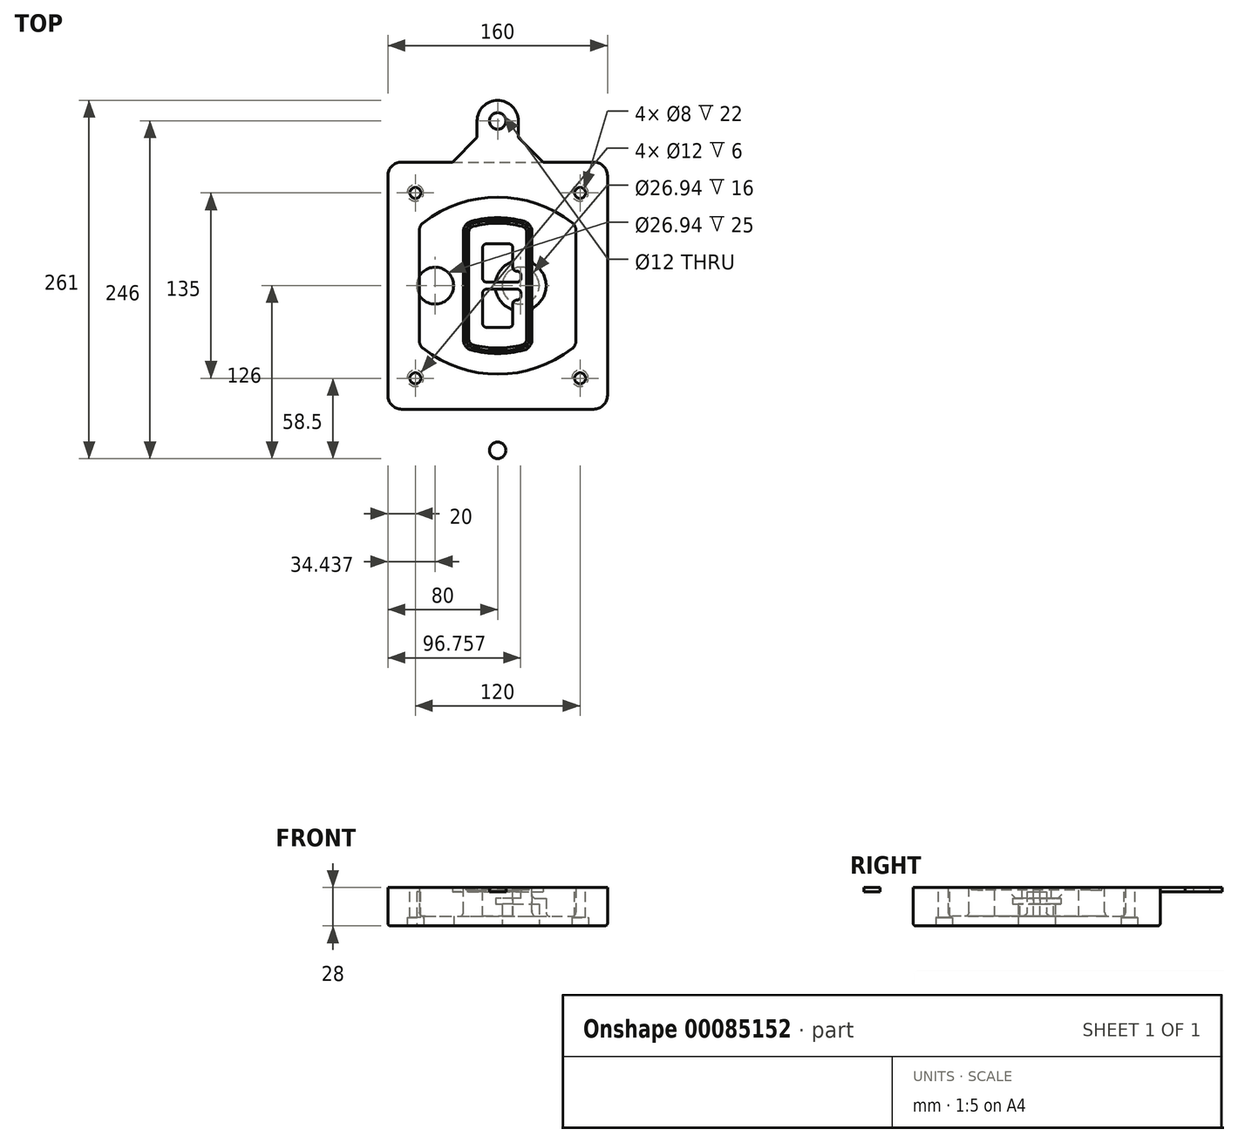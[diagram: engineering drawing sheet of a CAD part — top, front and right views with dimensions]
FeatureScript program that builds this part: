
annotation { "Feature Type Name" : "Feature", "Feature Type Description" : "" }
export const myFeature = defineFeature(function(context is Context, id is Id, definition is map)
    precondition{}
    {
        {
            var Q0;
            Q0=qCreatedBy(makeId("Top.planeOp"),FACE);
            var sketch = newSketch(context, id + "F0", { "sketchPlane" : qUnion([Q0])});
            skPoint(sketch, "E0.rect.middle", {"position": v(0, 0) * mm});
            skLineSegment(sketch, "E1.bottom", {"start": v(-70, -90) * mm, "end": v(70, -90) * mm});
            skLineSegment(sketch, "E1.top", {"start": v(-70, 90) * mm, "end": v(70, 90) * mm});
            skLineSegment(sketch, "E1.left", {"start": v(-80, -80) * mm, "end": v(-80, 80) * mm});
            skLineSegment(sketch, "E1.right", {"start": v(80, -80) * mm, "end": v(80, 80) * mm});
            skLineSegment(sketch, "E2", {"start": v(-80, 90) * mm, "end": v(80, -90) * mm, "construction": true});
            skLineSegment(sketch, "E3", {"start": v(80, 90) * mm, "end": v(-80, -90) * mm, "construction": true});
            skCircle(sketch, "E4", {"center": v(-60, 67.5) * mm, "radius": 4 * mm});
            skCircle(sketch, "E5", {"center": v(60, 67.5) * mm, "radius": 4 * mm});
            skCircle(sketch, "E6", {"center": v(60, -67.5) * mm, "radius": 4 * mm});
            skCircle(sketch, "E7", {"center": v(-60, -67.5) * mm, "radius": 4 * mm});
            skLineSegment(sketch, "E8", {"start": v(-60, 67.5) * mm, "end": v(60, 67.5) * mm, "construction": true});
            skLineSegment(sketch, "E9", {"start": v(60, 67.5) * mm, "end": v(60, -67.5) * mm, "construction": true});
            skLineSegment(sketch, "E10", {"start": v(60, -67.5) * mm, "end": v(-60, -67.5) * mm, "construction": true});
            skLineSegment(sketch, "E11", {"start": v(-60, -67.5) * mm, "end": v(-60, 67.5) * mm, "construction": true});
            skLineSegment(sketch, "E12", {"start": v(-60, 40.3) * mm, "end": v(-60, -40.3) * mm});
            skLineSegment(sketch, "E13", {"start": v(60, 40.3) * mm, "end": v(60, -40.3) * mm});
            skArc(sketch, "E14", {"start": v(56.15, 48.18) * mm, "mid": v(0, 67.5) * mm, "end": v(-56.15, 48.18) * mm});
            skArc(sketch, "E15", {"start": v(-56.15, -48.18) * mm, "mid": v(0, -67.5) * mm, "end": v(56.15, -48.18) * mm});
            skLineSegment(sketch, "E16", {"start": v(-60, 0) * mm, "end": v(60, 0) * mm, "construction": true});
            skPoint(sketch, "E17.visualSharp", {"position": v(-60, -45) * mm});
            skArc(sketch, "E17.filletArc", {"start": v(-60, -40.3) * mm, "mid": v(-58.99, -44.68) * mm, "end": v(-56.15, -48.18) * mm});
            skPoint(sketch, "E18.visualSharp", {"position": v(-60, 45) * mm});
            skArc(sketch, "E18.filletArc", {"start": v(-56.15, 48.18) * mm, "mid": v(-58.99, 44.68) * mm, "end": v(-60, 40.3) * mm});
            skPoint(sketch, "E19.visualSharp", {"position": v(60, 45) * mm});
            skArc(sketch, "E19.filletArc", {"start": v(60, 40.3) * mm, "mid": v(58.99, 44.68) * mm, "end": v(56.15, 48.18) * mm});
            skPoint(sketch, "E20.visualSharp", {"position": v(60, -45) * mm});
            skArc(sketch, "E20.filletArc", {"start": v(56.15, -48.18) * mm, "mid": v(58.99, -44.68) * mm, "end": v(60, -40.3) * mm});
            skPoint(sketch, "E21.visualSharp", {"position": v(-80, 90) * mm});
            skArc(sketch, "E21.filletArc", {"start": v(-70, 90) * mm, "mid": v(-77.07, 87.07) * mm, "end": v(-80, 80) * mm});
            skPoint(sketch, "E22.visualSharp", {"position": v(80, 90) * mm});
            skArc(sketch, "E22.filletArc", {"start": v(80, 80) * mm, "mid": v(77.07, 87.07) * mm, "end": v(70, 90) * mm});
            skPoint(sketch, "E23.visualSharp", {"position": v(80, -90) * mm});
            skArc(sketch, "E23.filletArc", {"start": v(70, -90) * mm, "mid": v(77.07, -87.07) * mm, "end": v(80, -80) * mm});
            skPoint(sketch, "E24.visualSharp", {"position": v(-80, -90) * mm});
            skArc(sketch, "E24.filletArc", {"start": v(-80, -80) * mm, "mid": v(-77.07, -87.07) * mm, "end": v(-70, -90) * mm});
            skArc(sketch, "E25.0", {"start": v(57, 40.3) * mm, "mid": v(56.3, 43.36) * mm, "end": v(54.3, 45.81) * mm});
            skLineSegment(sketch, "E25.1", {"start": v(57, 40.3) * mm, "end": v(57, -40.3) * mm});
            skArc(sketch, "E25.2", {"start": v(54.3, -45.81) * mm, "mid": v(56.3, -43.36) * mm, "end": v(57, -40.3) * mm});
            skArc(sketch, "E25.3", {"start": v(-54.3, -45.81) * mm, "mid": v(0, -64.5) * mm, "end": v(54.3, -45.81) * mm});
            skArc(sketch, "E25.4", {"start": v(-57, -40.3) * mm, "mid": v(-56.3, -43.36) * mm, "end": v(-54.3, -45.81) * mm});
            skArc(sketch, "E25.5", {"start": v(54.3, 45.81) * mm, "mid": v(0, 64.5) * mm, "end": v(-54.3, 45.81) * mm});
            skLineSegment(sketch, "E25.6", {"start": v(-57, 40.3) * mm, "end": v(-57, -40.3) * mm});
            skArc(sketch, "E25.7", {"start": v(-54.3, 45.81) * mm, "mid": v(-56.3, 43.36) * mm, "end": v(-57, 40.3) * mm});
            skArc(sketch, "E26.0", {"start": v(-58.62, 51.33) * mm, "mid": v(-62.58, 46.43) * mm, "end": v(-64, 40.3) * mm});
            skArc(sketch, "E26.1", {"start": v(58.62, 51.33) * mm, "mid": v(0, 71.5) * mm, "end": v(-58.62, 51.33) * mm});
            skArc(sketch, "E26.2", {"start": v(64, 40.3) * mm, "mid": v(62.58, 46.43) * mm, "end": v(58.62, 51.33) * mm});
            skLineSegment(sketch, "E26.3", {"start": v(64, 40.3) * mm, "end": v(64, -40.3) * mm});
            skArc(sketch, "E26.4", {"start": v(58.62, -51.33) * mm, "mid": v(62.58, -46.43) * mm, "end": v(64, -40.3) * mm});
            skLineSegment(sketch, "E26.5", {"start": v(-64, 40.3) * mm, "end": v(-64, -40.3) * mm});
            skArc(sketch, "E26.6", {"start": v(-58.62, -51.33) * mm, "mid": v(0, -71.5) * mm, "end": v(58.62, -51.33) * mm});
            skArc(sketch, "E26.7", {"start": v(-64, -40.3) * mm, "mid": v(-62.58, -46.43) * mm, "end": v(-58.62, -51.33) * mm});
            skSolve(sketch);
        }
        {
            var Q0;
            Q0=makeQuery(id+"F0.imprint","IMPRINT",FACE,{"disambiguationData":[TD([[makeQuery(id+"F0.imprint","IMPRINT",EDGE,{"derivedFrom":sQuery(id+"F0.wireOp",EDGE,"E1.bottom")}),1.0]])]});
            var Q1;
            Q1=makeQuery(id+"F0.imprint","IMPRINT",FACE,{"disambiguationData":[TD([[makeQuery(id+"F0.imprint","IMPRINT",EDGE,{"derivedFrom":sQuery(id+"F0.wireOp",EDGE,"E12")}),1.0]])]});
            var Q2;
            Q2=makeQuery(id+"F0.imprint","IMPRINT",FACE,{"disambiguationData":[TD([[makeQuery(id+"F0.imprint","IMPRINT",EDGE,{"derivedFrom":sQuery(id+"F0.wireOp",EDGE,"E25.0")}),1.0]])]});
            var Q3;
            Q3=makeQuery(id+"F0.imprint","IMPRINT",FACE,{"disambiguationData":[TD([[makeQuery(id+"F0.imprint","IMPRINT",EDGE,{"derivedFrom":sQuery(id+"F0.wireOp",EDGE,"E12")}),-1.0]])]});
            extrude(context, id + "F1", {"entities" : qUnion([Q0, Q1, Q2, Q3]), "oppositeDirection" : true, "depth" : 25 * mm});
        }
        {
            var Q0;
            Q0=makeQuery(id+"F0.imprint","IMPRINT",FACE,{"disambiguationData":[TD([[makeQuery(id+"F0.imprint","IMPRINT",EDGE,{"derivedFrom":sQuery(id+"F0.wireOp",EDGE,"E12")}),1.0]])]});
            extrude(context, id + "F2", {"entities" : qUnion([Q0]), "operationType" : NewBodyOperationType.ADD, "depth" : 3 * mm});
        }
        {
            var Q0;
            Q0=makeQuery(id+"F0.imprint","IMPRINT",FACE,{"disambiguationData":[TD([[makeQuery(id+"F0.imprint","IMPRINT",EDGE,{"derivedFrom":sQuery(id+"F0.wireOp",EDGE,"E25.0")}),1.0]])]});
            extrude(context, id + "F3", {"entities" : qUnion([Q0]), "operationType" : NewBodyOperationType.REMOVE, "oppositeDirection" : true, "depth" : 18 * mm});
        }
        {
            var Q0;
            Q0=makeQuery(id+"F2.opExtrude","CAP_FACE",FACE,{"disambiguationData":[OSD([sQuery(id+"F0.wireOp",EDGE,"E12"),sQuery(id+"F0.wireOp",EDGE,"E13"),sQuery(id+"F0.wireOp",EDGE,"E14"),sQuery(id+"F0.wireOp",EDGE,"E15"),sQuery(id+"F0.wireOp",EDGE,"E17.filletArc"),sQuery(id+"F0.wireOp",EDGE,"E18.filletArc"),sQuery(id+"F0.wireOp",EDGE,"E19.filletArc"),sQuery(id+"F0.wireOp",EDGE,"E20.filletArc"),sQuery(id+"F0.wireOp",EDGE,"E25.0"),sQuery(id+"F0.wireOp",EDGE,"E25.1"),sQuery(id+"F0.wireOp",EDGE,"E25.2"),sQuery(id+"F0.wireOp",EDGE,"E25.3"),sQuery(id+"F0.wireOp",EDGE,"E25.4"),sQuery(id+"F0.wireOp",EDGE,"E25.5"),sQuery(id+"F0.wireOp",EDGE,"E25.6"),sQuery(id+"F0.wireOp",EDGE,"E25.7")])],"isStart":false});
            var sketch = newSketch(context, id + "F4", { "sketchPlane" : qUnion([Q0])});
            skArc(sketch, "E27.0", {"start": v(-19.08, -46.97) * mm, "mid": v(0, -49.5) * mm, "end": v(19.08, -46.97) * mm});
            skArc(sketch, "E28.0", {"start": v(19.08, 46.97) * mm, "mid": v(0, 49.5) * mm, "end": v(-19.08, 46.97) * mm});
            skLineSegment(sketch, "E29", {"start": v(-25, 39.25) * mm, "end": v(-25, -39.25) * mm});
            skLineSegment(sketch, "E30", {"start": v(25, 39.25) * mm, "end": v(25, -39.25) * mm});
            skLineSegment(sketch, "E31", {"start": v(-25, 45.1) * mm, "end": v(25, 45.1) * mm, "construction": true});
            skLineSegment(sketch, "E32", {"start": v(-25, -45.1) * mm, "end": v(25, -45.1) * mm, "construction": true});
            skPoint(sketch, "E33.visualSharp", {"position": v(-25, 45.1) * mm});
            skArc(sketch, "E33.filletArc", {"start": v(-19.08, 46.97) * mm, "mid": v(-23.35, 44.11) * mm, "end": v(-25, 39.25) * mm});
            skPoint(sketch, "E34.visualSharp", {"position": v(25, 45.1) * mm});
            skArc(sketch, "E34.filletArc", {"start": v(25, 39.25) * mm, "mid": v(23.35, 44.11) * mm, "end": v(19.08, 46.97) * mm});
            skPoint(sketch, "E35.visualSharp", {"position": v(25, -45.1) * mm});
            skArc(sketch, "E35.filletArc", {"start": v(19.08, -46.97) * mm, "mid": v(23.35, -44.11) * mm, "end": v(25, -39.25) * mm});
            skPoint(sketch, "E36.visualSharp", {"position": v(-25, -45.1) * mm});
            skArc(sketch, "E36.filletArc", {"start": v(-25, -39.25) * mm, "mid": v(-23.35, -44.11) * mm, "end": v(-19.08, -46.97) * mm});
            skArc(sketch, "E37.0", {"start": v(54.3, 45.81) * mm, "mid": v(0, 64.5) * mm, "end": v(-54.3, 45.81) * mm});
            skArc(sketch, "E37.1", {"start": v(-54.3, 45.81) * mm, "mid": v(-56.3, 43.36) * mm, "end": v(-57, 40.3) * mm});
            skLineSegment(sketch, "E37.2", {"start": v(-57, 40.3) * mm, "end": v(-57, -40.3) * mm});
            skArc(sketch, "E37.3", {"start": v(-57, -40.3) * mm, "mid": v(-56.3, -43.36) * mm, "end": v(-54.3, -45.81) * mm});
            skArc(sketch, "E37.4", {"start": v(-54.3, -45.81) * mm, "mid": v(0, -64.5) * mm, "end": v(54.3, -45.81) * mm});
            skArc(sketch, "E37.5", {"start": v(54.3, -45.81) * mm, "mid": v(56.3, -43.36) * mm, "end": v(57, -40.3) * mm});
            skLineSegment(sketch, "E37.6", {"start": v(57, 40.3) * mm, "end": v(57, -40.3) * mm});
            skArc(sketch, "E37.7", {"start": v(57, 40.3) * mm, "mid": v(56.3, 43.36) * mm, "end": v(54.3, 45.81) * mm});
            skLineSegment(sketch, "E38.0", {"start": v(23, 39.25) * mm, "end": v(23, -39.25) * mm});
            skArc(sketch, "E38.1", {"start": v(18.56, -45.04) * mm, "mid": v(21.76, -42.9) * mm, "end": v(23, -39.25) * mm});
            skArc(sketch, "E38.2", {"start": v(-18.56, -45.04) * mm, "mid": v(0, -47.5) * mm, "end": v(18.56, -45.04) * mm});
            skArc(sketch, "E38.3", {"start": v(-23, -39.25) * mm, "mid": v(-21.76, -42.9) * mm, "end": v(-18.56, -45.04) * mm});
            skLineSegment(sketch, "E38.4", {"start": v(-23, 39.25) * mm, "end": v(-23, -39.25) * mm});
            skArc(sketch, "E38.5", {"start": v(23, 39.25) * mm, "mid": v(21.76, 42.9) * mm, "end": v(18.56, 45.04) * mm});
            skArc(sketch, "E38.6", {"start": v(-18.56, 45.04) * mm, "mid": v(-21.76, 42.9) * mm, "end": v(-23, 39.25) * mm});
            skArc(sketch, "E38.7", {"start": v(18.56, 45.04) * mm, "mid": v(0, 47.5) * mm, "end": v(-18.56, 45.04) * mm});
            skArc(sketch, "E39.0", {"start": v(21, 39.25) * mm, "mid": v(20.18, 41.68) * mm, "end": v(18.04, 43.1) * mm});
            skLineSegment(sketch, "E39.1", {"start": v(21, 39.25) * mm, "end": v(21, -39.25) * mm});
            skArc(sketch, "E39.2", {"start": v(18.04, -43.1) * mm, "mid": v(20.18, -41.68) * mm, "end": v(21, -39.25) * mm});
            skArc(sketch, "E39.3", {"start": v(-18.04, -43.1) * mm, "mid": v(0, -45.5) * mm, "end": v(18.04, -43.1) * mm});
            skArc(sketch, "E39.4", {"start": v(-21, -39.25) * mm, "mid": v(-20.18, -41.68) * mm, "end": v(-18.04, -43.1) * mm});
            skArc(sketch, "E39.5", {"start": v(18.04, 43.1) * mm, "mid": v(0, 45.5) * mm, "end": v(-18.04, 43.1) * mm});
            skLineSegment(sketch, "E39.6", {"start": v(-21, 39.25) * mm, "end": v(-21, -39.25) * mm});
            skArc(sketch, "E39.7", {"start": v(-18.04, 43.1) * mm, "mid": v(-20.18, 41.68) * mm, "end": v(-21, 39.25) * mm});
            skLineSegment(sketch, "E40", {"start": v(-25, 0) * mm, "end": v(25, 0) * mm, "construction": true});
            skLineSegment(sketch, "E41", {"start": v(-11, 5.5) * mm, "end": v(-11, 27.5) * mm});
            skLineSegment(sketch, "E42", {"start": v(-8, 30.5) * mm, "end": v(8, 30.5) * mm});
            skLineSegment(sketch, "E43", {"start": v(11, 27.5) * mm, "end": v(11, 13.5) * mm});
            skLineSegment(sketch, "E44", {"start": v(14, 10.5) * mm, "end": v(14, 10.5) * mm});
            skLineSegment(sketch, "E45", {"start": v(17, 7.5) * mm, "end": v(17, 5.5) * mm});
            skLineSegment(sketch, "E46", {"start": v(14, 2.5) * mm, "end": v(-8, 2.5) * mm});
            skPoint(sketch, "E47.visualSharp", {"position": v(-11, 30.5) * mm});
            skArc(sketch, "E47.filletArc", {"start": v(-8, 30.5) * mm, "mid": v(-10.12, 29.62) * mm, "end": v(-11, 27.5) * mm});
            skPoint(sketch, "E48.visualSharp", {"position": v(11, 30.5) * mm});
            skArc(sketch, "E48.filletArc", {"start": v(11, 27.5) * mm, "mid": v(10.12, 29.62) * mm, "end": v(8, 30.5) * mm});
            skPoint(sketch, "E49.visualSharp", {"position": v(11, 10.5) * mm});
            skArc(sketch, "E49.filletArc", {"start": v(11, 13.5) * mm, "mid": v(11.88, 11.38) * mm, "end": v(14, 10.5) * mm});
            skPoint(sketch, "E50.visualSharp", {"position": v(17, 10.5) * mm});
            skArc(sketch, "E50.filletArc", {"start": v(17, 7.5) * mm, "mid": v(16.12, 9.62) * mm, "end": v(14, 10.5) * mm});
            skPoint(sketch, "E51.visualSharp", {"position": v(17, 2.5) * mm});
            skArc(sketch, "E51.filletArc", {"start": v(14, 2.5) * mm, "mid": v(16.12, 3.38) * mm, "end": v(17, 5.5) * mm});
            skPoint(sketch, "E52.visualSharp", {"position": v(-11, 2.5) * mm});
            skArc(sketch, "E52.filletArc", {"start": v(-11, 5.5) * mm, "mid": v(-10.12, 3.38) * mm, "end": v(-8, 2.5) * mm});
            skLineSegment(sketch, "E53.0.MirrorCS", {"start": v(14, -2.5) * mm, "end": v(-8, -2.5) * mm});
            skArc(sketch, "E54.0.MirrorCS", {"start": v(-11, -5.5) * mm, "mid": v(-10.12, -3.38) * mm, "end": v(-8, -2.5) * mm});
            skLineSegment(sketch, "E55.0.MirrorCS", {"start": v(-11, -5.5) * mm, "end": v(-11, -27.5) * mm});
            skArc(sketch, "E56.0.MirrorCS", {"start": v(-8, -30.5) * mm, "mid": v(-10.12, -29.62) * mm, "end": v(-11, -27.5) * mm});
            skLineSegment(sketch, "E57.0.MirrorCS", {"start": v(-8, -30.5) * mm, "end": v(8, -30.5) * mm});
            skArc(sketch, "E58.0.MirrorCS", {"start": v(11, -27.5) * mm, "mid": v(10.12, -29.62) * mm, "end": v(8, -30.5) * mm});
            skLineSegment(sketch, "E59.0.MirrorCS", {"start": v(11, -27.5) * mm, "end": v(11, -13.5) * mm});
            skArc(sketch, "E60.0.MirrorCS", {"start": v(11, -13.5) * mm, "mid": v(11.88, -11.38) * mm, "end": v(14, -10.5) * mm});
            skArc(sketch, "E61.0.MirrorCS", {"start": v(17, -7.5) * mm, "mid": v(16.12, -9.62) * mm, "end": v(14, -10.5) * mm});
            skLineSegment(sketch, "E62.0.MirrorCS", {"start": v(17, -7.5) * mm, "end": v(17, -5.5) * mm});
            skArc(sketch, "E63.0.MirrorCS", {"start": v(14, -2.5) * mm, "mid": v(16.12, -3.38) * mm, "end": v(17, -5.5) * mm});
            skSolve(sketch);
        }
        {
            var Q0;
            Q0=makeQuery(id+"F4.imprint","IMPRINT",FACE,{"disambiguationData":[TD([[makeQuery(id+"F4.imprint","IMPRINT",EDGE,{"derivedFrom":sQuery(id+"F4.wireOp",EDGE,"E27.0")}),1.0]])]});
            var Q1;
            Q1=makeQuery(id+"F4.imprint","IMPRINT",FACE,{"disambiguationData":[TD([[makeQuery(id+"F4.imprint","IMPRINT",EDGE,{"derivedFrom":sQuery(id+"F4.wireOp",EDGE,"E38.0")}),-1.0]])]});
            var Q2;
            Q2=makeQuery(id+"F4.imprint","IMPRINT",FACE,{"disambiguationData":[TD([[makeQuery(id+"F4.imprint","IMPRINT",EDGE,{"derivedFrom":sQuery(id+"F4.wireOp",EDGE,"E39.0")}),1.0]])]});
            extrude(context, id + "F5", {"entities" : qUnion([Q0, Q1, Q2]), "operationType" : NewBodyOperationType.ADD, "endBound" : BoundingType.UP_TO_NEXT, "oppositeDirection" : true, "depth" : 25 * mm});
        }
        {
            var Q0;
            Q0=makeQuery(id+"F4.imprint","IMPRINT",FACE,{"disambiguationData":[TD([[makeQuery(id+"F4.imprint","IMPRINT",EDGE,{"derivedFrom":sQuery(id+"F4.wireOp",EDGE,"E38.0")}),-1.0]])]});
            extrude(context, id + "F6", {"entities" : qUnion([Q0]), "operationType" : NewBodyOperationType.REMOVE, "oppositeDirection" : true, "depth" : 2 * mm});
        }
        {
            var Q0;
            Q0=makeQuery(id+"F1.opExtrude","CAP_FACE",FACE,{"disambiguationData":[OSD([sQuery(id+"F0.wireOp",EDGE,"E1.bottom"),sQuery(id+"F0.wireOp",EDGE,"E1.top"),sQuery(id+"F0.wireOp",EDGE,"E1.left"),sQuery(id+"F0.wireOp",EDGE,"E1.right"),sQuery(id+"F0.wireOp",EDGE,"E4"),sQuery(id+"F0.wireOp",EDGE,"E5"),sQuery(id+"F0.wireOp",EDGE,"E6"),sQuery(id+"F0.wireOp",EDGE,"E7"),sQuery(id+"F0.wireOp",EDGE,"E21.filletArc"),sQuery(id+"F0.wireOp",EDGE,"E22.filletArc"),sQuery(id+"F0.wireOp",EDGE,"E23.filletArc"),sQuery(id+"F0.wireOp",EDGE,"E24.filletArc")])],"isStart":false});
            var sketch = newSketch(context, id + "F7", { "sketchPlane" : qUnion([Q0])});
            skCircle(sketch, "E64", {"center": v(16.76, 0) * mm, "radius": 13.47 * mm});
            skCircle(sketch, "E65", {"center": v(-45.56, 0) * mm, "radius": 13.47 * mm});
            skLineSegment(sketch, "E66", {"start": v(80, 0) * mm, "end": v(-80, 0) * mm});
            skCircle(sketch, "E67", {"center": v(16.76, 0) * mm, "radius": 18.47 * mm});
            skCircle(sketch, "E68", {"center": v(60, -67.5) * mm, "radius": 6 * mm});
            skCircle(sketch, "E69", {"center": v(-60, -67.5) * mm, "radius": 6 * mm});
            skCircle(sketch, "E70", {"center": v(-60, 67.5) * mm, "radius": 6 * mm});
            skCircle(sketch, "E71", {"center": v(60, 67.5) * mm, "radius": 6 * mm});
            skSolve(sketch);
        }
        {
            var Q0;
            {var subQ1=sQuery(id+"F7.wireOp",EDGE,"E66");var subQ4=sQuery(id+"F7.wireOp",EDGE,"E64");var subQ6=makeQuery(id+"F7.imprint","INTERSECT",VERTEX,{"disambiguationData":[OD(0.0)],"derivedFrom":[subQ4,subQ1]});Q0=makeQuery(id+"F7.imprint","IMPRINT",FACE,{"disambiguationData":[TD([[makeQuery(id+"F7.imprint","IMPRINT",EDGE,{"disambiguationData":[TD([[subQ6,-1.0]])],"derivedFrom":subQ4}),-1.0]])]});}
            var Q1;
            {var subQ0=sQuery(id+"F7.wireOp",EDGE,"E66");var subQ1=sQuery(id+"F7.wireOp",EDGE,"E64");var subQ3=makeQuery(id+"F7.imprint","INTERSECT",VERTEX,{"disambiguationData":[OD(0.0)],"derivedFrom":[subQ1,subQ0]});Q1=makeQuery(id+"F7.imprint","IMPRINT",FACE,{"disambiguationData":[TD([[makeQuery(id+"F7.imprint","IMPRINT",EDGE,{"disambiguationData":[TD([[subQ3,-1.0]])],"derivedFrom":subQ1}),1.0]])]});}
            var Q2;
            {var subQ0=sQuery(id+"F7.wireOp",EDGE,"E66");var subQ1=sQuery(id+"F7.wireOp",EDGE,"E64");var subQ3=makeQuery(id+"F7.imprint","INTERSECT",VERTEX,{"disambiguationData":[OD(0.0)],"derivedFrom":[subQ1,subQ0]});Q2=makeQuery(id+"F7.imprint","IMPRINT",FACE,{"disambiguationData":[TD([[makeQuery(id+"F7.imprint","IMPRINT",EDGE,{"disambiguationData":[TD([[subQ3,1.0]])],"derivedFrom":subQ1}),1.0]])]});}
            var Q3;
            {var subQ1=sQuery(id+"F7.wireOp",EDGE,"E66");var subQ4=sQuery(id+"F7.wireOp",EDGE,"E64");var subQ6=makeQuery(id+"F7.imprint","INTERSECT",VERTEX,{"disambiguationData":[OD(0.0)],"derivedFrom":[subQ4,subQ1]});Q3=makeQuery(id+"F7.imprint","IMPRINT",FACE,{"disambiguationData":[TD([[makeQuery(id+"F7.imprint","IMPRINT",EDGE,{"disambiguationData":[TD([[subQ6,1.0]])],"derivedFrom":subQ4}),-1.0]])]});}
            extrude(context, id + "F8", {"entities" : qUnion([Q0, Q1, Q2, Q3]), "operationType" : NewBodyOperationType.ADD, "oppositeDirection" : true, "depth" : 20 * mm});
        }
        {
            var Q0;
            {var subQ0=sQuery(id+"F7.wireOp",EDGE,"E66");var subQ1=sQuery(id+"F7.wireOp",EDGE,"E64");var subQ3=makeQuery(id+"F7.imprint","INTERSECT",VERTEX,{"disambiguationData":[OD(0.0)],"derivedFrom":[subQ1,subQ0]});Q0=makeQuery(id+"F7.imprint","IMPRINT",FACE,{"disambiguationData":[TD([[makeQuery(id+"F7.imprint","IMPRINT",EDGE,{"disambiguationData":[TD([[subQ3,-1.0]])],"derivedFrom":subQ1}),1.0]])]});}
            var Q1;
            {var subQ0=sQuery(id+"F7.wireOp",EDGE,"E66");var subQ1=sQuery(id+"F7.wireOp",EDGE,"E64");var subQ3=makeQuery(id+"F7.imprint","INTERSECT",VERTEX,{"disambiguationData":[OD(0.0)],"derivedFrom":[subQ1,subQ0]});Q1=makeQuery(id+"F7.imprint","IMPRINT",FACE,{"disambiguationData":[TD([[makeQuery(id+"F7.imprint","IMPRINT",EDGE,{"disambiguationData":[TD([[subQ3,1.0]])],"derivedFrom":subQ1}),1.0]])]});}
            extrude(context, id + "F9", {"entities" : qUnion([Q0, Q1]), "operationType" : NewBodyOperationType.REMOVE, "oppositeDirection" : true, "depth" : 16 * mm});
        }
        {
            var Q0;
            {var subQ0=sQuery(id+"F7.wireOp",EDGE,"E66");var subQ1=sQuery(id+"F7.wireOp",EDGE,"E65");var subQ3=makeQuery(id+"F7.imprint","INTERSECT",VERTEX,{"disambiguationData":[OD(0.0)],"derivedFrom":[subQ1,subQ0]});Q0=makeQuery(id+"F7.imprint","IMPRINT",FACE,{"disambiguationData":[TD([[makeQuery(id+"F7.imprint","IMPRINT",EDGE,{"disambiguationData":[TD([[subQ3,-1.0]])],"derivedFrom":subQ1}),1.0]])]});}
            var Q1;
            {var subQ0=sQuery(id+"F7.wireOp",EDGE,"E66");var subQ1=sQuery(id+"F7.wireOp",EDGE,"E65");var subQ3=makeQuery(id+"F7.imprint","INTERSECT",VERTEX,{"disambiguationData":[OD(0.0)],"derivedFrom":[subQ1,subQ0]});Q1=makeQuery(id+"F7.imprint","IMPRINT",FACE,{"disambiguationData":[TD([[makeQuery(id+"F7.imprint","IMPRINT",EDGE,{"disambiguationData":[TD([[subQ3,1.0]])],"derivedFrom":subQ1}),1.0]])]});}
            extrude(context, id + "F10", {"entities" : qUnion([Q0, Q1]), "operationType" : NewBodyOperationType.REMOVE, "oppositeDirection" : true, "depth" : 25 * mm});
        }
        {
            var Q0;
            Q0=makeQuery(id+"F7.imprint","IMPRINT",FACE,{"disambiguationData":[TD([[makeQuery(id+"F7.imprint","IMPRINT",EDGE,{"derivedFrom":sQuery(id+"F7.wireOp",EDGE,"E68")}),1.0]])]});
            var Q1;
            Q1=makeQuery(id+"F7.imprint","IMPRINT",FACE,{"disambiguationData":[TD([[makeQuery(id+"F7.imprint","IMPRINT",EDGE,{"derivedFrom":makeQuery(id+"F1.opExtrude","CAP_EDGE",EDGE,{"disambiguationData":[OSD([sQuery(id+"F0.wireOp",EDGE,"E5")])],"isStart":false})}),-1.0]])]});
            var Q2;
            Q2=makeQuery(id+"F7.imprint","IMPRINT",FACE,{"disambiguationData":[TD([[makeQuery(id+"F7.imprint","IMPRINT",EDGE,{"derivedFrom":sQuery(id+"F7.wireOp",EDGE,"E69")}),1.0]])]});
            var Q3;
            Q3=makeQuery(id+"F7.imprint","IMPRINT",FACE,{"disambiguationData":[TD([[makeQuery(id+"F7.imprint","IMPRINT",EDGE,{"derivedFrom":makeQuery(id+"F1.opExtrude","CAP_EDGE",EDGE,{"disambiguationData":[OSD([sQuery(id+"F0.wireOp",EDGE,"E4")])],"isStart":false})}),-1.0]])]});
            var Q4;
            Q4=makeQuery(id+"F7.imprint","IMPRINT",FACE,{"disambiguationData":[TD([[makeQuery(id+"F7.imprint","IMPRINT",EDGE,{"derivedFrom":sQuery(id+"F7.wireOp",EDGE,"E70")}),1.0]])]});
            var Q5;
            Q5=makeQuery(id+"F7.imprint","IMPRINT",FACE,{"disambiguationData":[TD([[makeQuery(id+"F7.imprint","IMPRINT",EDGE,{"derivedFrom":makeQuery(id+"F1.opExtrude","CAP_EDGE",EDGE,{"disambiguationData":[OSD([sQuery(id+"F0.wireOp",EDGE,"E7")])],"isStart":false})}),-1.0]])]});
            var Q6;
            Q6=makeQuery(id+"F7.imprint","IMPRINT",FACE,{"disambiguationData":[TD([[makeQuery(id+"F7.imprint","IMPRINT",EDGE,{"derivedFrom":sQuery(id+"F7.wireOp",EDGE,"E71")}),1.0]])]});
            var Q7;
            Q7=makeQuery(id+"F7.imprint","IMPRINT",FACE,{"disambiguationData":[TD([[makeQuery(id+"F7.imprint","IMPRINT",EDGE,{"derivedFrom":makeQuery(id+"F1.opExtrude","CAP_EDGE",EDGE,{"disambiguationData":[OSD([sQuery(id+"F0.wireOp",EDGE,"E6")])],"isStart":false})}),-1.0]])]});
            extrude(context, id + "F11", {"entities" : qUnion([Q0, Q1, Q2, Q3, Q4, Q5, Q6, Q7]), "operationType" : NewBodyOperationType.REMOVE, "oppositeDirection" : true, "depth" : 6 * mm});
        }
        {
            var Q0;
            Q0=makeQuery(id+"F9.boolean.opBoolean","COPY",FACE,{"derivedFrom":makeQuery(id+"F9.opExtrude","CAP_FACE",FACE,{"disambiguationData":[OSD([sQuery(id+"F7.wireOp",EDGE,"E64")])],"isStart":false})});
            var sketch = newSketch(context, id + "F12", { "sketchPlane" : qUnion([Q0])});
            skArc(sketch, "E72.0", {"start": v(11, 17.55) * mm, "mid": v(2.57, 11.82) * mm, "end": v(-1.54, 2.5) * mm});
            skArc(sketch, "E72.1", {"start": v(-1.54, -2.5) * mm, "mid": v(2.57, -11.82) * mm, "end": v(11, -17.55) * mm});
            skLineSegment(sketch, "E73", {"start": v(-1.54, -2.5) * mm, "end": v(14, -2.5) * mm});
            skLineSegment(sketch, "E74.0", {"start": v(14, 2.5) * mm, "end": v(-1.54, 2.5) * mm});
            skArc(sketch, "E74.1", {"start": v(14, 2.5) * mm, "mid": v(16.12, 3.38) * mm, "end": v(17, 5.5) * mm});
            skLineSegment(sketch, "E74.2", {"start": v(17, 7.5) * mm, "end": v(17, 5.5) * mm});
            skArc(sketch, "E74.3", {"start": v(17, 7.5) * mm, "mid": v(16.12, 9.62) * mm, "end": v(14, 10.5) * mm});
            skArc(sketch, "E74.4", {"start": v(11, 13.5) * mm, "mid": v(11.88, 11.38) * mm, "end": v(14, 10.5) * mm});
            skLineSegment(sketch, "E74.5", {"start": v(11, 17.55) * mm, "end": v(11, 13.5) * mm});
            skLineSegment(sketch, "E74.7", {"start": v(14, -2.5) * mm, "end": v(-1.54, -2.5) * mm});
            skArc(sketch, "E74.8", {"start": v(14, -2.5) * mm, "mid": v(16.12, -3.38) * mm, "end": v(17, -5.5) * mm});
            skLineSegment(sketch, "E74.9", {"start": v(17, -7.5) * mm, "end": v(17, -5.5) * mm});
            skArc(sketch, "E74.10", {"start": v(17, -7.5) * mm, "mid": v(16.12, -9.62) * mm, "end": v(14, -10.5) * mm});
            skArc(sketch, "E74.11", {"start": v(11, -13.5) * mm, "mid": v(11.88, -11.38) * mm, "end": v(14, -10.5) * mm});
            skLineSegment(sketch, "E74.12", {"start": v(11, -17.55) * mm, "end": v(11, -13.5) * mm});
            skPoint(sketch, "E75.orphan", {"position": v(11, -27.5) * mm});
            skPoint(sketch, "E76.orphan", {"position": v(-8, -2.5) * mm});
            skPoint(sketch, "E77.orphan", {"position": v(-8, 2.5) * mm});
            skPoint(sketch, "E78.orphan", {"position": v(11, 27.5) * mm});
            skSolve(sketch);
        }
        {
            var Q0;
            {var subQ7=sQuery(id+"F12.wireOp",EDGE,"E72.0");var subQ14=sQuery(id+"F12.wireOp",EDGE,"E72.1");var subQ16=sQuery(id+"F12.wireOp",EDGE,"E74.1");var subQ18=sQuery(id+"F12.wireOp",EDGE,"E74.8");Q0=qUnion([makeQuery(id+"F12.imprint","IMPRINT",FACE,{"disambiguationData":[TD([[makeQuery(id+"F12.imprint","IMPRINT",EDGE,{"derivedFrom":subQ7}),1.0]])]}),makeQuery(id+"F12.imprint","IMPRINT",FACE,{"disambiguationData":[TD([[makeQuery(id+"F12.imprint","IMPRINT",EDGE,{"derivedFrom":subQ14}),1.0]])]}),makeQuery(id+"F12.imprint","IMPRINT",FACE,{"disambiguationData":[TD([[makeQuery(id+"F12.imprint","IMPRINT",EDGE,{"derivedFrom":subQ16}),1.0]])]}),makeQuery(id+"F12.imprint","IMPRINT",FACE,{"disambiguationData":[TD([[makeQuery(id+"F12.imprint","IMPRINT",EDGE,{"derivedFrom":subQ18}),-1.0]])]})]);}
            var Q1;
            Q1=makeQuery(id+"F5.boolean.opBoolean","SPLIT",FACE,{"disambiguationData":[TD([makeQuery(id+"F5.opExtrude","SWEPT_FACE",FACE,{"disambiguationData":[OSD([sQuery(id+"F4.wireOp",EDGE,"E41")])]})])],"derivedFrom":makeQuery(id+"F3.boolean.opBoolean","COPY",FACE,{"derivedFrom":makeQuery(id+"F3.opExtrude","CAP_FACE",FACE,{"disambiguationData":[OSD([sQuery(id+"F0.wireOp",EDGE,"E25.0"),sQuery(id+"F0.wireOp",EDGE,"E25.1"),sQuery(id+"F0.wireOp",EDGE,"E25.2"),sQuery(id+"F0.wireOp",EDGE,"E25.3"),sQuery(id+"F0.wireOp",EDGE,"E25.4"),sQuery(id+"F0.wireOp",EDGE,"E25.5"),sQuery(id+"F0.wireOp",EDGE,"E25.6"),sQuery(id+"F0.wireOp",EDGE,"E25.7")])],"isStart":false})})});
            extrude(context, id + "F13", {"entities" : qUnion([Q0]), "operationType" : NewBodyOperationType.REMOVE, "endBound" : BoundingType.UP_TO_SURFACE, "endBoundEntityFace" : qUnion([Q1]), "depth" : 25 * mm});
        }
        {
            var Q0;
            Q0=makeQuery(id+"F3.boolean.opBoolean","COPY",EDGE,{"derivedFrom":makeQuery(id+"F3.opExtrude","CAP_EDGE",EDGE,{"disambiguationData":[OSD([sQuery(id+"F0.wireOp",EDGE,"E25.6")])],"isStart":false})});
            var Q1;
            Q1=makeQuery(id+"F8.boolean.opBoolean","INTERSECT",EDGE,{"derivedFrom":[makeQuery(id+"F5.opExtrude","SWEPT_FACE",FACE,{"disambiguationData":[OSD([sQuery(id+"F4.wireOp",EDGE,"E30")])]}),makeQuery(id+"F8.opExtrude","CAP_FACE",FACE,{"disambiguationData":[OSD([sQuery(id+"F7.wireOp",EDGE,"E67")])],"isStart":false})]});
            var Q2;
            Q2=makeQuery(id+"F8.boolean.opBoolean","INTERSECT",EDGE,{"disambiguationData":[OD(1.0)],"derivedFrom":[makeQuery(id+"F5.opExtrude","SWEPT_FACE",FACE,{"disambiguationData":[OSD([sQuery(id+"F4.wireOp",EDGE,"E30")])]}),makeQuery(id+"F8.opExtrude","SWEPT_FACE",FACE,{"disambiguationData":[OSD([sQuery(id+"F7.wireOp",EDGE,"E67")])]})]});
            var Q3;
            {var subQ0=sQuery(id+"F4.wireOp",EDGE,"E30");Q3=makeQuery(id+"F8.boolean.opBoolean","SPLIT",EDGE,{"disambiguationData":[TD([makeQuery(id+"F5.opExtrude","SWEPT_FACE",FACE,{"disambiguationData":[OSD([sQuery(id+"F4.wireOp",EDGE,"E35.filletArc")])]})])],"derivedFrom":makeQuery(id+"F5.opExtrude","CAP_EDGE",EDGE,{"disambiguationData":[OSD([subQ0])],"isStart":false})});}
            var Q4;
            {var subQ0=sQuery(id+"F0.wireOp",EDGE,"E25.7");var subQ1=sQuery(id+"F0.wireOp",EDGE,"E25.1");var subQ2=sQuery(id+"F0.wireOp",EDGE,"E25.6");var subQ3=sQuery(id+"F0.wireOp",EDGE,"E25.5");var subQ4=sQuery(id+"F0.wireOp",EDGE,"E25.4");var subQ5=sQuery(id+"F0.wireOp",EDGE,"E25.0");var subQ6=sQuery(id+"F0.wireOp",EDGE,"E25.2");var subQ7=sQuery(id+"F0.wireOp",EDGE,"E25.3");Q4=makeQuery(id+"F8.boolean.opBoolean","INTERSECT",EDGE,{"derivedFrom":[makeQuery(id+"F5.boolean.opBoolean","SPLIT",FACE,{"disambiguationData":[TD([makeQuery(id+"F2.opExtrude","SWEPT_FACE",FACE,{"disambiguationData":[OSD([subQ5])]})])],"derivedFrom":makeQuery(id+"F3.boolean.opBoolean","COPY",FACE,{"derivedFrom":makeQuery(id+"F3.opExtrude","CAP_FACE",FACE,{"disambiguationData":[OSD([subQ5,subQ1,subQ6,subQ7,subQ4,subQ3,subQ2,subQ0])],"isStart":false})})}),makeQuery(id+"F8.opExtrude","SWEPT_FACE",FACE,{"disambiguationData":[OSD([sQuery(id+"F7.wireOp",EDGE,"E67")])]})]});}
            var Q5;
            Q5=makeQuery(id+"F8.boolean.opBoolean","INTERSECT",EDGE,{"disambiguationData":[OD(0.0)],"derivedFrom":[makeQuery(id+"F5.opExtrude","SWEPT_FACE",FACE,{"disambiguationData":[OSD([sQuery(id+"F4.wireOp",EDGE,"E30")])]}),makeQuery(id+"F8.opExtrude","SWEPT_FACE",FACE,{"disambiguationData":[OSD([sQuery(id+"F7.wireOp",EDGE,"E67")])]})]});
            fillet(context, id + "F14", {"entities" : qUnion([Q0, Q1, Q2, Q3, Q4, Q5]), "radius" : 3 * mm, "tangentPropagation" : true, "allowEdgeOverflow" : false});
        }
        {
            var Q0;
            Q0=makeQuery(id+"F1.opExtrude","CAP_EDGE",EDGE,{"disambiguationData":[OSD([sQuery(id+"F0.wireOp",EDGE,"E1.bottom")])],"isStart":false});
            fillet(context, id + "F15", {"entities" : qUnion([Q0]), "radius" : 2 * mm, "tangentPropagation" : true, "allowEdgeOverflow" : false});
        }
        {
            var Q0;
            {var subQ0=sQuery(id+"F0.wireOp",EDGE,"E22.filletArc");var subQ1=sQuery(id+"F0.wireOp",EDGE,"E7");var subQ2=sQuery(id+"F0.wireOp",EDGE,"E6");var subQ3=sQuery(id+"F0.wireOp",EDGE,"E5");var subQ4=sQuery(id+"F0.wireOp",EDGE,"E4");var subQ5=sQuery(id+"F0.wireOp",EDGE,"E1.bottom");var subQ6=sQuery(id+"F0.wireOp",EDGE,"E21.filletArc");var subQ7=sQuery(id+"F0.wireOp",EDGE,"E1.top");var subQ8=sQuery(id+"F0.wireOp",EDGE,"E1.left");var subQ9=sQuery(id+"F0.wireOp",EDGE,"E1.right");var subQ10=sQuery(id+"F0.wireOp",EDGE,"E23.filletArc");var subQ11=sQuery(id+"F0.wireOp",EDGE,"E24.filletArc");Q0=makeQuery(id+"F2.boolean.opBoolean","SPLIT",FACE,{"disambiguationData":[TD([makeQuery(id+"F1.opExtrude","SWEPT_FACE",FACE,{"disambiguationData":[OSD([subQ5])]})])],"derivedFrom":makeQuery(id+"F1.opExtrude","CAP_FACE",FACE,{"disambiguationData":[OSD([subQ5,subQ7,subQ8,subQ9,subQ4,subQ3,subQ2,subQ1,subQ6,subQ0,subQ10,subQ11])],"isStart":true})});}
            var sketch = newSketch(context, id + "F16", { "sketchPlane" : qUnion([Q0])});
            skLineSegment(sketch, "E79", {"start": v(0, 90) * mm, "end": v(0, 120) * mm, "construction": true});
            skCircle(sketch, "E80", {"center": v(0, 120) * mm, "radius": 6 * mm});
            skArc(sketch, "E81", {"start": v(-15, 120) * mm, "mid": v(0, 135) * mm, "end": v(15, 120) * mm});
            skLineSegment(sketch, "E82", {"start": v(-15, 120) * mm, "end": v(-15, 108) * mm});
            skLineSegment(sketch, "E83.MirrorCS", {"start": v(15, 120) * mm, "end": v(15, 108) * mm});
            skLineSegment(sketch, "E84", {"start": v(-15, 108) * mm, "end": v(-33, 90) * mm});
            skLineSegment(sketch, "E85.MirrorCS", {"start": v(15, 108) * mm, "end": v(33, 90) * mm});
            skLineSegment(sketch, "E86", {"start": v(-80, 0) * mm, "end": v(80, 0) * mm, "construction": true});
            skCircle(sketch, "E87.MirrorC", {"center": v(0, -120) * mm, "radius": 6 * mm});
            skArc(sketch, "E88.MirrorCS", {"start": v(-15, -120) * mm, "mid": v(0, -135) * mm, "end": v(15, -120) * mm});
            skLineSegment(sketch, "E89.MirrorCS", {"start": v(-15, -108) * mm, "end": v(-33, -90) * mm});
            skLineSegment(sketch, "E90.MirrorCS", {"start": v(15, -108) * mm, "end": v(33, -90) * mm});
            skLineSegment(sketch, "E91.MirrorCS", {"start": v(15, -120) * mm, "end": v(15, -108) * mm});
            skLineSegment(sketch, "E92.MirrorCS", {"start": v(-15, -120) * mm, "end": v(-15, -108) * mm});
            skSolve(sketch);
        }
        {
            var Q0;
            Q0=makeQuery(id+"F16.imprint","IMPRINT",FACE,{"disambiguationData":[TD([[makeQuery(id+"F16.imprint","IMPRINT",EDGE,{"derivedFrom":sQuery(id+"F16.wireOp",EDGE,"E80")}),-1.0]])]});
            var Q1;
            Q1=makeQuery(id+"F16.imprint","IMPRINT",FACE,{"disambiguationData":[TD([[makeQuery(id+"F16.imprint","IMPRINT",EDGE,{"derivedFrom":sQuery(id+"F16.wireOp",EDGE,"E87.MirrorC")}),1.0]])]});
            var Q2;
            Q2=makeQuery(id+"F16.imprint","IMPRINT",FACE,{"disambiguationData":[TD([[makeQuery(id+"F16.imprint","IMPRINT",EDGE,{"derivedFrom":makeQuery(id+"F1.opExtrude","CAP_EDGE",EDGE,{"disambiguationData":[OSD([sQuery(id+"F0.wireOp",EDGE,"E1.left")])],"isStart":true})}),-1.0]])]});
            var Q3;
            Q3=makeQuery(id+"F2.opExtrude","CAP_FACE",FACE,{"disambiguationData":[OSD([sQuery(id+"F0.wireOp",EDGE,"E12"),sQuery(id+"F0.wireOp",EDGE,"E13"),sQuery(id+"F0.wireOp",EDGE,"E14"),sQuery(id+"F0.wireOp",EDGE,"E15"),sQuery(id+"F0.wireOp",EDGE,"E17.filletArc"),sQuery(id+"F0.wireOp",EDGE,"E18.filletArc"),sQuery(id+"F0.wireOp",EDGE,"E19.filletArc"),sQuery(id+"F0.wireOp",EDGE,"E20.filletArc"),sQuery(id+"F0.wireOp",EDGE,"E25.0"),sQuery(id+"F0.wireOp",EDGE,"E25.1"),sQuery(id+"F0.wireOp",EDGE,"E25.2"),sQuery(id+"F0.wireOp",EDGE,"E25.3"),sQuery(id+"F0.wireOp",EDGE,"E25.4"),sQuery(id+"F0.wireOp",EDGE,"E25.5"),sQuery(id+"F0.wireOp",EDGE,"E25.6"),sQuery(id+"F0.wireOp",EDGE,"E25.7")])],"isStart":false});
            extrude(context, id + "F17", {"entities" : qUnion([Q0, Q1, Q2]), "operationType" : NewBodyOperationType.ADD, "endBound" : BoundingType.UP_TO_SURFACE, "endBoundEntityFace" : qUnion([Q3]), "depth" : 25 * mm});
        }
    });
